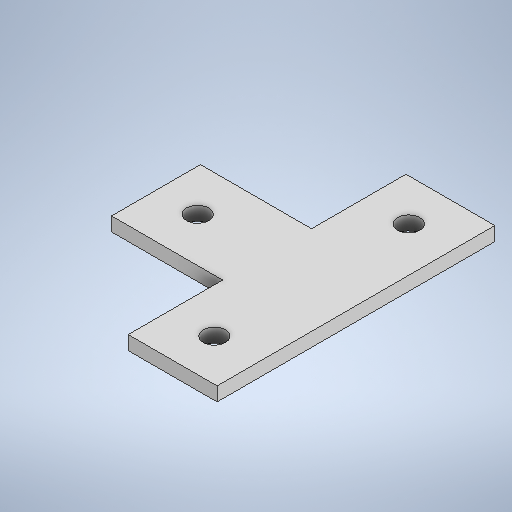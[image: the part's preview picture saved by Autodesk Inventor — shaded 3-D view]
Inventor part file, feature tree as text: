
AUTODESK INVENTOR PART (.ipt)
format: ipt  version: 2025.1 (Build 291241000, 241)  size: 238,592 bytes
history: native  units: in
note: dims shown in document units (in); Inventor stores cm internally (conversion verified against a paired STEP export)
features: extrude x1, sketch x1
ambient origin geometry x8: Origin, YZ Plane, XZ Plane, XY Plane, X Axis, Y Axis, Z Axis, Center Point
bodies: Solid1 (feature_tree)
feature tree (2):
  extrude  "Extrusion1"  Depth=2.5in
  sketch  "Sketch1"  dims[d0=0.8in d1=2.5in d2=1.0in d3=0.4in d4=0.4in d5=0.375in d6=0.375in d7=0.2in d8=0.2in d9=0.375in d10=0.2in d11=0.125in d12=0.0in]
